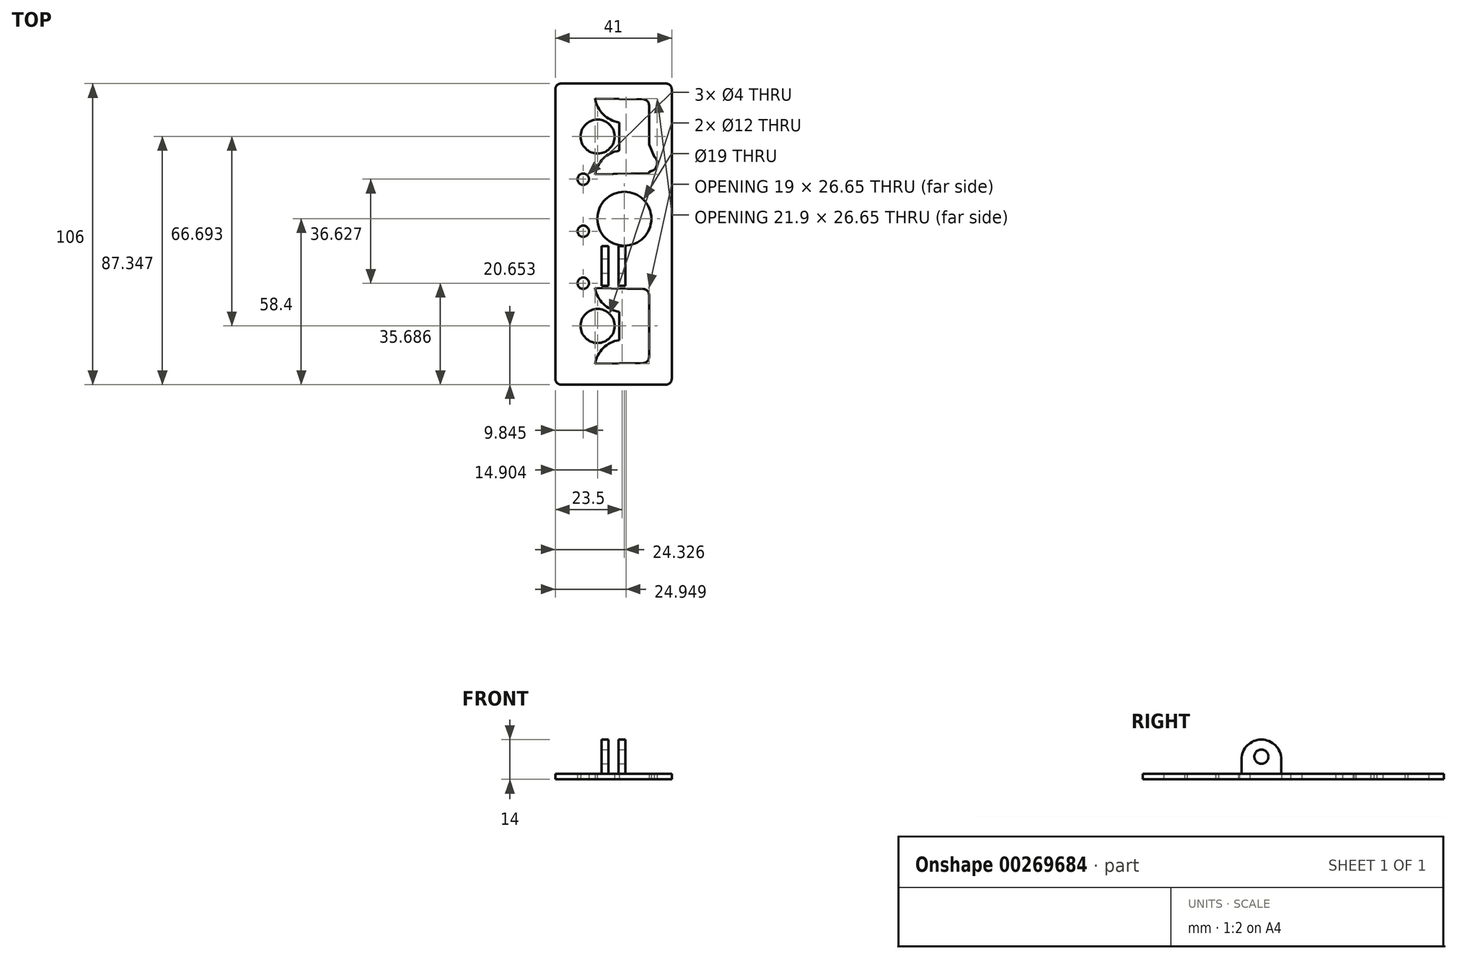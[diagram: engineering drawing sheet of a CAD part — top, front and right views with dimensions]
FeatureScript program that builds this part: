
annotation { "Feature Type Name" : "Feature", "Feature Type Description" : "" }
export const myFeature = defineFeature(function(context is Context, id is Id, definition is map)
    precondition{}
    {
        {
            var Q0;
            Q0=qCreatedBy(makeId("Top.planeOp"),FACE);
            var sketch = newSketch(context, id + "F0", { "sketchPlane" : qUnion([Q0])});
            skLineSegment(sketch, "E0.bottom", {"start": v(-20.5, 57.25) * mm, "end": v(20.5, 57.25) * mm});
            skLineSegment(sketch, "E0.top", {"start": v(-20.5, -48.75) * mm, "end": v(20.5, -48.75) * mm});
            skLineSegment(sketch, "E0.left", {"start": v(-20.5, 57.25) * mm, "end": v(-20.5, -48.75) * mm});
            skLineSegment(sketch, "E0.right", {"start": v(20.5, 57.25) * mm, "end": v(20.5, -48.75) * mm});
            skArc(sketch, "E1", {"start": v(-6.5, 51.92) * mm, "mid": v(-3.6, 46.37) * mm, "end": v(2, 43.6) * mm});
            skLineSegment(sketch, "E2", {"start": v(2, 43.6) * mm, "end": v(2, 33.6) * mm});
            skLineSegment(sketch, "E3", {"start": v(-10.68, 38.6) * mm, "end": v(23.63, 38.6) * mm, "construction": true});
            skArc(sketch, "E4.MirrorCS", {"start": v(-6.5, 25.27) * mm, "mid": v(-3.6, 30.82) * mm, "end": v(2, 33.6) * mm});
            skCircle(sketch, "E5", {"center": v(-1.11, 47.1) * mm, "radius": 1.5 * mm});
            skCircle(sketch, "E6.MirrorC", {"center": v(-1.11, 30.1) * mm, "radius": 1.5 * mm});
            skCircle(sketch, "E7", {"center": v(-5.6, 38.6) * mm, "radius": 6 * mm});
            skLineSegment(sketch, "E8", {"start": v(-26.97, 5.25) * mm, "end": v(22.04, 5.25) * mm, "construction": true});
            skCircle(sketch, "E9.MirrorC", {"center": v(-1.11, -19.6) * mm, "radius": 1.5 * mm});
            skArc(sketch, "E10.MirrorCS", {"start": v(-6.5, -14.77) * mm, "mid": v(-3.6, -20.32) * mm, "end": v(2, -23.1) * mm});
            skLineSegment(sketch, "E11.MirrorCS", {"start": v(2, -33.1) * mm, "end": v(2, -23.1) * mm});
            skArc(sketch, "E12.MirrorCS", {"start": v(-6.5, -41.42) * mm, "mid": v(-3.6, -35.87) * mm, "end": v(2, -33.1) * mm});
            skCircle(sketch, "E13.MirrorC", {"center": v(-1.11, -36.6) * mm, "radius": 1.5 * mm});
            skCircle(sketch, "E14.MirrorC", {"center": v(-5.6, -28.1) * mm, "radius": 6 * mm});
            skLineSegment(sketch, "E15", {"start": v(-2.67, -11.83) * mm, "end": v(-2.67, -42.97) * mm, "construction": true});
            skLineSegment(sketch, "E16", {"start": v(12.5, -15.13) * mm, "end": v(12.5, -41.13) * mm});
            skLineSegment(sketch, "E17", {"start": v(12.5, -41.13) * mm, "end": v(-6.5, -41.42) * mm});
            skLineSegment(sketch, "E18", {"start": v(12.5, -15.13) * mm, "end": v(-6.5, -14.77) * mm});
            skLineSegment(sketch, "E19.MirrorCS", {"start": v(12.5, 25.63) * mm, "end": v(-6.5, 25.27) * mm});
            skLineSegment(sketch, "E20.MirrorCS", {"start": v(12.5, 25.63) * mm, "end": v(12.5, 51.63) * mm});
            skLineSegment(sketch, "E21.MirrorCS", {"start": v(12.5, 51.63) * mm, "end": v(-6.5, 51.92) * mm});
            skCircle(sketch, "E22", {"center": v(3.83, 9.65) * mm, "radius": 9.5 * mm});
            skCircle(sketch, "E23", {"center": v(9.5, 35.25) * mm, "radius": 3 * mm});
            skCircle(sketch, "E24", {"center": v(12.4, 29.25) * mm, "radius": 3 * mm});
            skCircle(sketch, "E25", {"center": v(-10.66, 5.25) * mm, "radius": 2 * mm});
            skCircle(sketch, "E26", {"center": v(-10.66, -13.06) * mm, "radius": 2 * mm});
            skCircle(sketch, "E27.MirrorC", {"center": v(-10.66, 23.56) * mm, "radius": 2 * mm});
            skLineSegment(sketch, "E28", {"start": v(7.11, 33.43) * mm, "end": v(9.69, 27.97) * mm});
            skLineSegment(sketch, "E29", {"start": v(14.36, 31.52) * mm, "end": v(12.26, 36.43) * mm});
            skLineSegment(sketch, "E30.bottom", {"start": v(1.75, 0) * mm, "end": v(4.25, 0) * mm});
            skLineSegment(sketch, "E30.top", {"start": v(1.75, -14) * mm, "end": v(4.25, -14) * mm});
            skLineSegment(sketch, "E30.left", {"start": v(1.75, 0) * mm, "end": v(1.75, -14) * mm});
            skLineSegment(sketch, "E30.right", {"start": v(4.25, 0) * mm, "end": v(4.25, -14) * mm});
            skLineSegment(sketch, "E31.MirrorCS", {"start": v(-1.75, 0) * mm, "end": v(-1.75, -14) * mm});
            skLineSegment(sketch, "E32.MirrorCS", {"start": v(-4.25, 0) * mm, "end": v(-4.25, -14) * mm});
            skLineSegment(sketch, "E33.MirrorCS", {"start": v(-1.75, -14) * mm, "end": v(-4.25, -14) * mm});
            skLineSegment(sketch, "E34.MirrorCS", {"start": v(-1.75, 0) * mm, "end": v(-4.25, 0) * mm});
            skSolve(sketch);
        }
        {
            var Q0;
            Q0=makeQuery(id+"F0.imprint","IMPRINT",FACE,{"disambiguationData":[TD([[makeQuery(id+"F0.imprint","IMPRINT",EDGE,{"derivedFrom":sQuery(id+"F0.wireOp",EDGE,"E0.bottom")}),-1.0]])]});
            extrude(context, id + "F1", {"entities" : qUnion([Q0]), "depth" : 2 * mm});
        }
        {
            var Q0;
            Q0=makeQuery(id+"F1.opExtrude","SWEPT_EDGE",EDGE,{"disambiguationData":[OSD([sQuery(id+"F0.wireOp",EDGE,"E0.top"),sQuery(id+"F0.wireOp",EDGE,"E0.right")])]});
            var Q1;
            Q1=makeQuery(id+"F1.opExtrude","SWEPT_EDGE",EDGE,{"disambiguationData":[OSD([sQuery(id+"F0.wireOp",EDGE,"E0.top"),sQuery(id+"F0.wireOp",EDGE,"E0.left")])]});
            var Q2;
            Q2=makeQuery(id+"F1.opExtrude","SWEPT_EDGE",EDGE,{"disambiguationData":[OSD([sQuery(id+"F0.wireOp",EDGE,"E16"),sQuery(id+"F0.wireOp",EDGE,"E18")])]});
            var Q3;
            Q3=makeQuery(id+"F1.opExtrude","SWEPT_EDGE",EDGE,{"disambiguationData":[OSD([sQuery(id+"F0.wireOp",EDGE,"E16"),sQuery(id+"F0.wireOp",EDGE,"E17")])]});
            var Q4;
            Q4=makeQuery(id+"F1.opExtrude","SWEPT_EDGE",EDGE,{"disambiguationData":[OSD([sQuery(id+"F0.wireOp",EDGE,"E20.MirrorCS"),sQuery(id+"F0.wireOp",EDGE,"E21.MirrorCS")])]});
            var Q5;
            Q5=makeQuery(id+"F1.opExtrude","SWEPT_EDGE",EDGE,{"disambiguationData":[OSD([sQuery(id+"F0.wireOp",EDGE,"E0.bottom"),sQuery(id+"F0.wireOp",EDGE,"E0.right")])]});
            var Q6;
            Q6=makeQuery(id+"F1.opExtrude","SWEPT_EDGE",EDGE,{"disambiguationData":[OSD([sQuery(id+"F0.wireOp",EDGE,"E0.bottom"),sQuery(id+"F0.wireOp",EDGE,"E0.left")])]});
            fillet(context, id + "F2", {"entities" : qUnion([Q0, Q1, Q2, Q3, Q4, Q5, Q6]), "radius" : 2 * mm, "tangentPropagation" : true, "allowEdgeOverflow" : false});
        }
        {
            var Q0;
            Q0=makeQuery(id+"F0.imprint","IMPRINT",FACE,{"disambiguationData":[TD([[makeQuery(id+"F0.imprint","IMPRINT",EDGE,{"derivedFrom":sQuery(id+"F0.wireOp",EDGE,"E31.MirrorCS")}),-1.0]])]});
            var Q1;
            Q1=makeQuery(id+"F0.imprint","IMPRINT",FACE,{"disambiguationData":[TD([[makeQuery(id+"F0.imprint","IMPRINT",EDGE,{"derivedFrom":sQuery(id+"F0.wireOp",EDGE,"E30.bottom")}),-1.0]])]});
            extrude(context, id + "F3", {"entities" : qUnion([Q0, Q1]), "operationType" : NewBodyOperationType.ADD, "depth" : 14 * mm});
        }
        {
            var Q0;
            Q0=makeQuery(id+"F3.opExtrude","CAP_EDGE",EDGE,{"disambiguationData":[OSD([sQuery(id+"F0.wireOp",EDGE,"E30.bottom")])],"isStart":false});
            var Q1;
            Q1=makeQuery(id+"F3.opExtrude","CAP_EDGE",EDGE,{"disambiguationData":[OSD([sQuery(id+"F0.wireOp",EDGE,"E30.top")])],"isStart":false});
            var Q2;
            Q2=makeQuery(id+"F3.opExtrude","CAP_EDGE",EDGE,{"disambiguationData":[OSD([sQuery(id+"F0.wireOp",EDGE,"E33.MirrorCS")])],"isStart":false});
            var Q3;
            Q3=makeQuery(id+"F3.opExtrude","CAP_EDGE",EDGE,{"disambiguationData":[OSD([sQuery(id+"F0.wireOp",EDGE,"E34.MirrorCS")])],"isStart":false});
            fillet(context, id + "F4", {"entities" : qUnion([Q0, Q1, Q2, Q3]), "radius" : 7 * mm, "tangentPropagation" : true, "allowEdgeOverflow" : false});
        }
        {
            var Q0;
            Q0=makeQuery(id+"F3.opExtrude","SWEPT_FACE",FACE,{"disambiguationData":[OSD([sQuery(id+"F0.wireOp",EDGE,"E30.right")])]});
            var sketch = newSketch(context, id + "F5", { "sketchPlane" : qUnion([Q0])});
            skCircle(sketch, "E35", {"center": v(-7, 8) * mm, "radius": 2.5 * mm});
            skPoint(sketch, "E35.centerSnap0", {"position": v(-7, 14) * mm});
            skSolve(sketch);
        }
        {
            var Q0;
            Q0=makeQuery(id+"F5.imprint","IMPRINT",FACE,{"disambiguationData":[TD([[makeQuery(id+"F5.imprint","IMPRINT",EDGE,{"derivedFrom":sQuery(id+"F5.wireOp",EDGE,"E35")}),1.0]])]});
            extrude(context, id + "F6", {"entities" : qUnion([Q0]), "operationType" : NewBodyOperationType.REMOVE, "oppositeDirection" : true, "depth" : 25 * mm});
        }
    });
